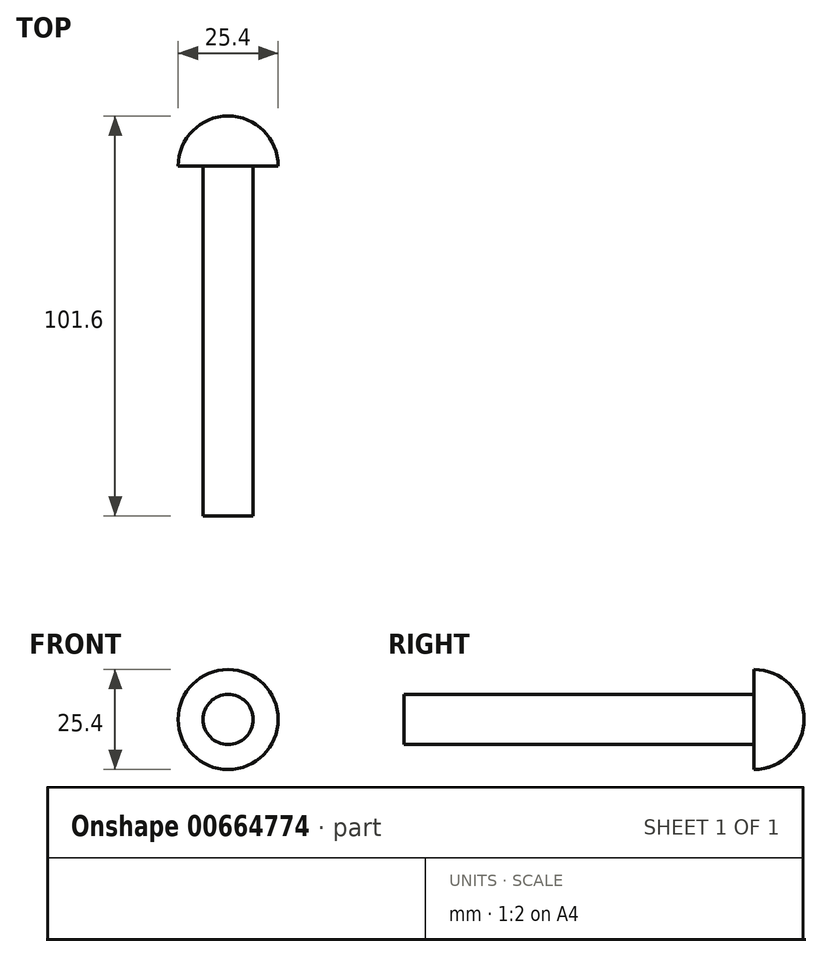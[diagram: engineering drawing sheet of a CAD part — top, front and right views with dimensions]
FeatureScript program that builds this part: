
annotation { "Feature Type Name" : "Feature", "Feature Type Description" : "" }
export const myFeature = defineFeature(function(context is Context, id is Id, definition is map)
    precondition{}
    {
        {
            var Q0;
            Q0=qCreatedBy(makeId("Front.planeOp"),FACE);
            var sketch = newSketch(context, id + "F0", { "sketchPlane" : qUnion([Q0])});
            skCircle(sketch, "E0", {"center": v(0, 0) * mm, "radius": 6.35 * mm});
            skSolve(sketch);
        }
        {
            var Q0;
            Q0 = qSketchRegion(id + "F0", true);
            extrude(context, id + "F1", {"entities" : qUnion([Q0]), "depth" : 101.6 * mm, "offsetDistance" : 25.4 * mm});
        }
        {
            var Q0;
            Q0=qCreatedBy(makeId("Front.planeOp"),FACE);
            var sketch = newSketch(context, id + "F2", { "sketchPlane" : qUnion([Q0])});
            skCircle(sketch, "E1", {"center": v(0, 0) * mm, "radius": 12.7 * mm});
            skSolve(sketch);
        }
        {
            var Q0;
            Q0=makeQuery(id+"F2.imprint","IMPRINT",FACE,{"disambiguationData":[TD([[makeQuery(id+"F2.imprint","IMPRINT",EDGE,{"derivedFrom":sQuery(id+"F2.wireOp",EDGE,"E1")}),1.0]])]});
            extrude(context, id + "F3", {"entities" : qUnion([Q0]), "operationType" : NewBodyOperationType.ADD, "depth" : 12.7 * mm, "offsetDistance" : 25.4 * mm});
        }
        {
            var Q0;
            Q0=makeQuery(id+"F3.opExtrude","CAP_EDGE",EDGE,{"disambiguationData":[OSD([sQuery(id+"F2.wireOp",EDGE,"E1")])],"isStart":true});
            fillet(context, id + "F4", {"entities" : qUnion([Q0]), "radius" : 12.7 * mm, "tangentPropagation" : true, "allowEdgeOverflow" : false});
        }
    });
